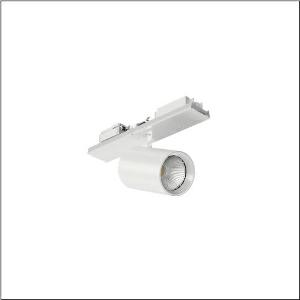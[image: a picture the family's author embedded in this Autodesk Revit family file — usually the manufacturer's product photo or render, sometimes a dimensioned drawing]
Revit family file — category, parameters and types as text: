
# Revit family: licross_r__spot_31_51sl147a45b_9b2d
name_source: partatom
category: Lighting Fixtures
units: mm (PartAtom-declared; Revit-internal decimal feet)

## family parameters
Cut with Voids When Loaded = No
Host = Face
Light Source = No
Part Type = Normal
Room Calculation Point = No
Round Connector Dimension = Use Diameter
Shared = No

## types (1)
- --- (1 x LED, 5250 lm, 42.4 W, 4000K)
    Apparent Load = 42 VA
    CIE Flux Codes = 93 97 100 100 100
    Color Rendering = 90
    Color Temperature = 4000K
    Default Elevation = 1800 mm
    Description = Licross® Spot 31, directional spotlight, light control with lens, of plastic, LED rated luminous flux: 5.250lm, light colour: 940, with plug, 3-pole, with phase selection, mains connection: 220..240V, AC, 50/60Hz, of aluminium, traffic white (RAL 9016), length: 140mm, diameter: 90mm, protection rating (complete): IP20, insulation class (complete): insulation class I (protective earthing), certification: CE, packaging unit: 1 piece
    Height = 175 mm
    Lamp = 1 x LED
    Lamp Light Flux = 5250 lm
    Lamp Power = 42.4 W
    Lamp count = 1
    Length = 90 mm
    Luminous efficacy = 124 lm/W
    Manufacturer = Siteco
    ModVariant = No
    Model = 51SL147A45B
    Mounting Place = Ceiling
    Mounting Type = Pendant
    Number of Poles = 1
    OnlyDefault = Yes
    Power Factor = 1
    Product Name = Licross® Spot 31
    Product group = directional spotlight
    ProductGroupID = 905
    Protection Class = Protection class I
    Protection Degree = IP 20
    RLX_Detail_Level = 1
    RLX_Emergency_Light_Flux = 0 lm
    RLX_Emergency_Type = 0
    RLX_Emergency_Type_DB = No
    RlxData = <blob elided: 14809 chars, md5=d0e9338f>
    Socket = socket
    Standby Power = 0 W
    System Light Flux = 5250 lm
    System Power = 42 W
    Type Comments = factory setting: luminous flux: 100 % | (ON | ON | ON) | 1050 mA
    Type Image = l_1245720.jpg
    URL = http://relux.com
    VarID = @adj_063687
    Voltage = 0 V
    Weight = 0.00 kg
    Width = 0 mm  [stored 0 ft]

note: [stored X ft] marks values corroborated as IEEE doubles in the binary element streams (Revit-internal decimal feet)

## geometry (parser evidence)
native form markers: Sweep x12
no freeform markers — native parametric forms only
